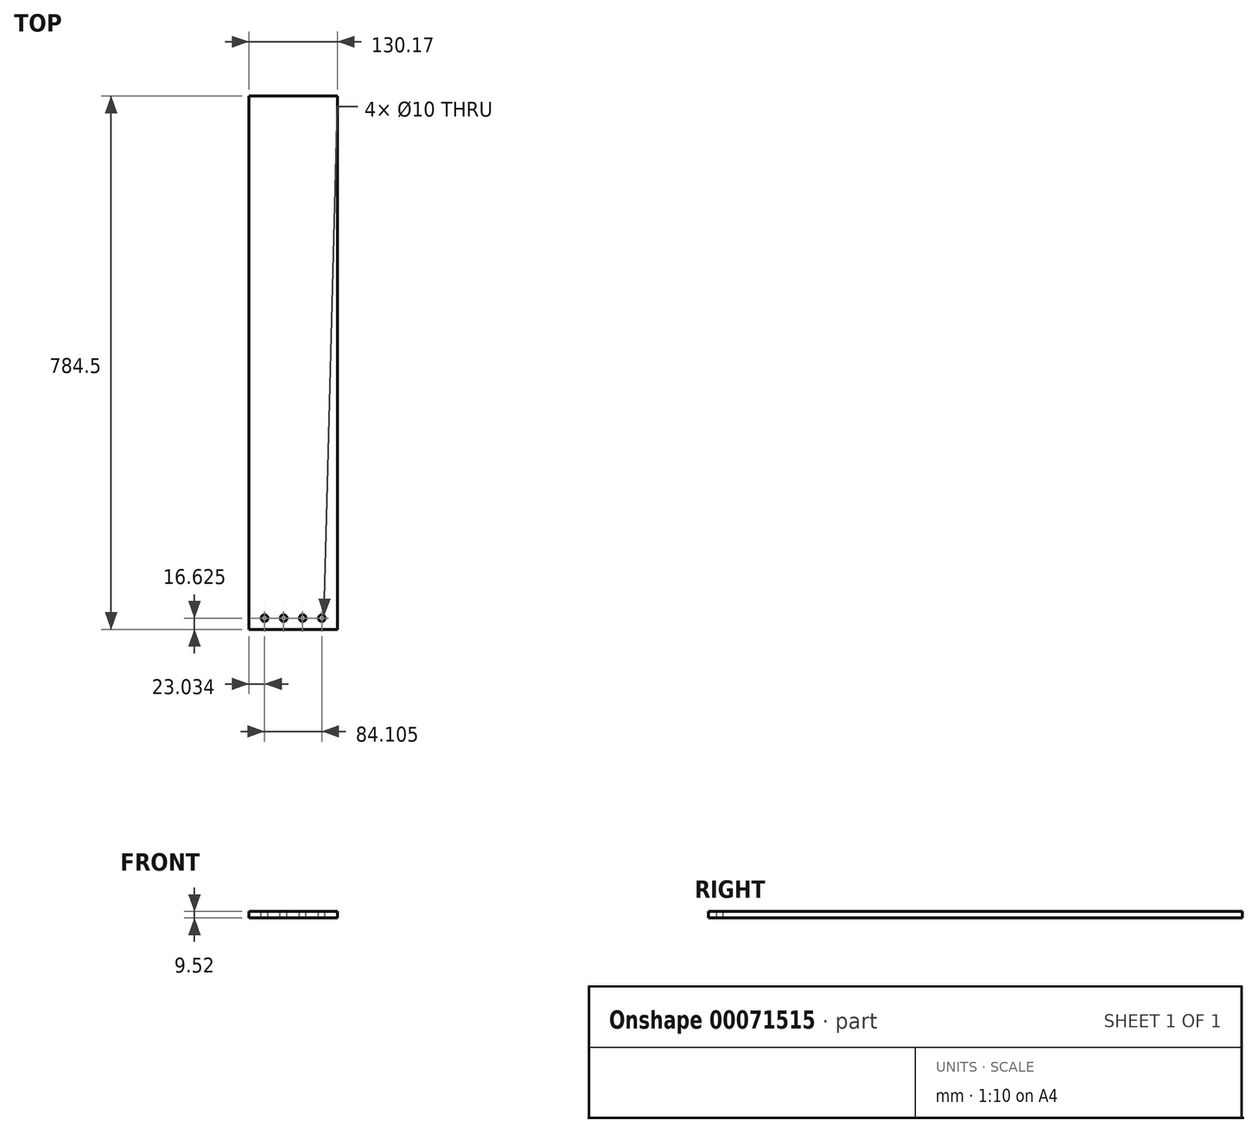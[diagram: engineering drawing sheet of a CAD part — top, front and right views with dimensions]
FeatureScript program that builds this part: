
annotation { "Feature Type Name" : "Feature", "Feature Type Description" : "" }
export const myFeature = defineFeature(function(context is Context, id is Id, definition is map)
    precondition{}
    {
        {
            var Q0;
            Q0=qCreatedBy(makeId("Front.planeOp"),FACE);
            var sketch = newSketch(context, id + "F0", { "sketchPlane" : qUnion([Q0])});
            skLineSegment(sketch, "E0.bottom", {"start": v(-78.85, -19.43) * mm, "end": v(51.32, -19.43) * mm});
            skLineSegment(sketch, "E1.top", {"start": v(-78.85, -28.95) * mm, "end": v(51.32, -28.95) * mm});
            skLineSegment(sketch, "E1.left", {"start": v(-78.85, -19.43) * mm, "end": v(-78.85, -28.95) * mm});
            skLineSegment(sketch, "E1.right", {"start": v(51.32, -19.43) * mm, "end": v(51.32, -28.95) * mm});
            skSolve(sketch);
        }
        {
            var Q0;
            Q0=makeQuery(id+"F0.imprint","IMPRINT",FACE,{"disambiguationData":[TD([[makeQuery(id+"F0.imprint","IMPRINT",EDGE,{"derivedFrom":sQuery(id+"F0.wireOp",EDGE,"E0.bottom")}),-1.0]])]});
            var Q1;
            Q1=makeQuery(id+"F0.imprint","IMPRINT",FACE,{"disambiguationData":[TD([[makeQuery(id+"F0.imprint","IMPRINT",EDGE,{"derivedFrom":sQuery(id+"F0.wireOp",EDGE,"E0.bottom")}),-1.0]])]});
            extrude(context, id + "F1", {"entities" : qUnion([Q0, Q1]), "depth" : 784.5 * mm});
        }
        {
            var Q0;
            Q0=makeQuery(id+"F1.opExtrude","SWEPT_FACE",FACE,{"disambiguationData":[OSD([sQuery(id+"F0.wireOp",EDGE,"E0.bottom")])]});
            var sketch = newSketch(context, id + "F2", { "sketchPlane" : qUnion([Q0])});
            skCircle(sketch, "E2", {"center": v(-55.82, -767.88) * mm, "radius": 5 * mm});
            skCircle(sketch, "E3.1.0.0", {"center": v(-27.78, -767.88) * mm, "radius": 5 * mm});
            skCircle(sketch, "E3.2.0.0", {"center": v(0.25, -767.88) * mm, "radius": 5 * mm});
            skLineSegment(sketch, "E3.direction1", {"start": v(-55.82, -767.88) * mm, "end": v(-27.78, -767.88) * mm, "construction": true});
            skCircle(sketch, "E4.0.3.0", {"center": v(28.29, -767.88) * mm, "radius": 5 * mm});
            skSolve(sketch);
        }
        {
            var Q0;
            Q0 = qSketchRegion(id + "F2", true);
            extrude(context, id + "F3", {"entities" : qUnion([Q0]), "operationType" : NewBodyOperationType.REMOVE, "oppositeDirection" : true, "depth" : 25 * mm});
        }
    });
